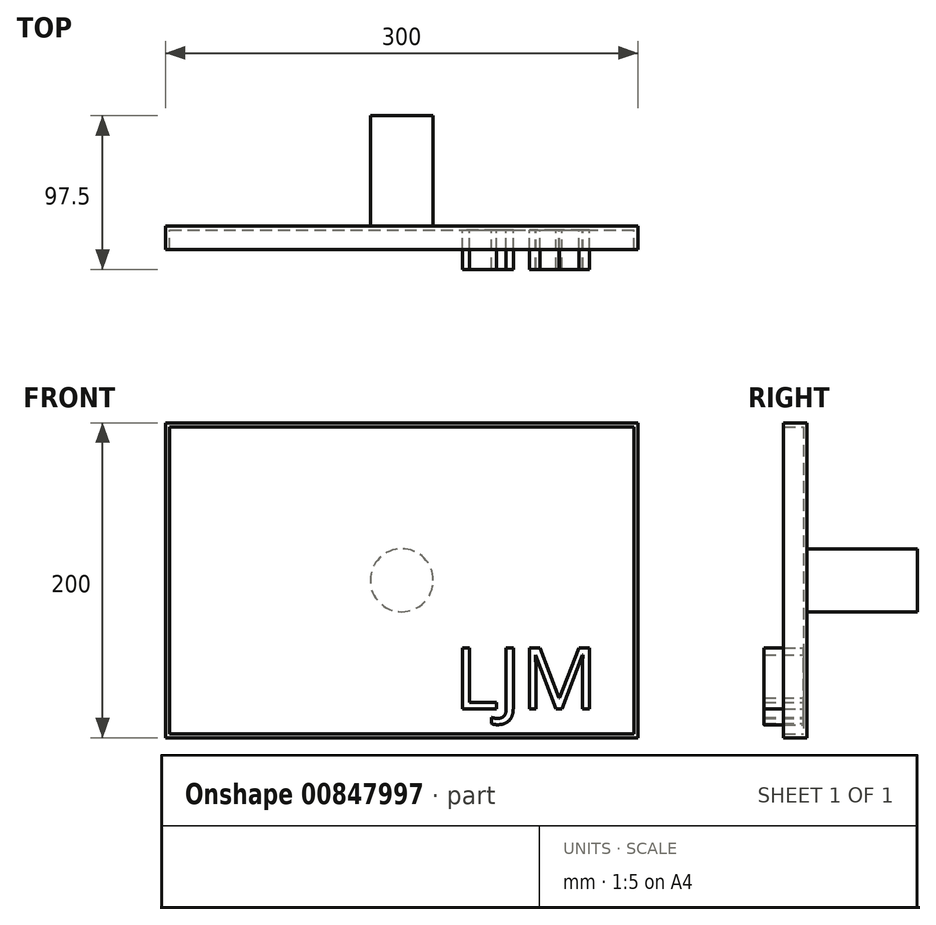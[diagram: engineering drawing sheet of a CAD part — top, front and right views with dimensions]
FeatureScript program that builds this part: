
annotation { "Feature Type Name" : "Feature", "Feature Type Description" : "" }
export const myFeature = defineFeature(function(context is Context, id is Id, definition is map)
    precondition{}
    {
        {
            var Q0;
            Q0=qCreatedBy(makeId("Front.planeOp"),FACE);
            var sketch = newSketch(context, id + "F0", { "sketchPlane" : qUnion([Q0])});
            skLineSegment(sketch, "E0.bottom", {"start": v(-150, 100) * mm, "end": v(150, 100) * mm});
            skLineSegment(sketch, "E0.top", {"start": v(-150, -100) * mm, "end": v(150, -100) * mm});
            skLineSegment(sketch, "E0.left", {"start": v(-150, 100) * mm, "end": v(-150, -100) * mm});
            skLineSegment(sketch, "E0.right", {"start": v(150, 100) * mm, "end": v(150, -100) * mm});
            skLineSegment(sketch, "E1", {"start": v(0, 0) * mm, "end": v(0, 116.1) * mm});
            skSolve(sketch);
        }
        {
            var Q0;
            Q0=makeQuery(id+"F0.imprint","IMPRINT",FACE,{"disambiguationData":[TD([[makeQuery(id+"F0.imprint","IMPRINT",EDGE,{"derivedFrom":sQuery(id+"F0.wireOp",EDGE,"E0.bottom")}),-1.0]])]});
            extrude(context, id + "F1", {"entities" : qUnion([Q0]), "depth" : 15 * mm, "offsetDistance" : 25 * mm});
        }
        {
            var Q0;
            Q0=makeQuery(id+"F1.opExtrude","CAP_FACE",FACE,{"disambiguationData":[OSD([sQuery(id+"F0.wireOp",EDGE,"E0.bottom"),sQuery(id+"F0.wireOp",EDGE,"E0.top"),sQuery(id+"F0.wireOp",EDGE,"E0.left"),sQuery(id+"F0.wireOp",EDGE,"E0.right")])],"isStart":false});
            shell(context, id + "F2", {"entities" : qUnion([Q0]), "thickness" : 2.5 * mm});
        }
        {
            var Q0;
            Q0=makeQuery(id+"F2.opShell","OFFSET_FACE",FACE,{"disambiguationData":[OSD([sQuery(id+"F0.wireOp",EDGE,"E0.bottom"),sQuery(id+"F0.wireOp",EDGE,"E0.top"),sQuery(id+"F0.wireOp",EDGE,"E0.left"),sQuery(id+"F0.wireOp",EDGE,"E0.right")])]});
            var sketch = newSketch(context, id + "F3", { "sketchPlane" : qUnion([Q0])});
            skText(sketch, "E2", { "text": "LJM", "fontName": "OpenSans-Regular.ttf"});
            const initialGuessF3  = {"E2": [0.03333, -0.08161, 1, 0, 0.03885]};
            skSetInitialGuess(sketch, initialGuessF3);
            skSolve(sketch);
        }
        {
            var Q0;
            Q0 = qSketchRegion(id + "F3", true);
            extrude(context, id + "F4", {"entities" : qUnion([Q0]), "operationType" : NewBodyOperationType.ADD, "depth" : 25 * mm, "offsetDistance" : 25 * mm});
        }
        {
            var Q0;
            Q0=makeQuery(id+"F1.opExtrude","CAP_FACE",FACE,{"disambiguationData":[OSD([sQuery(id+"F0.wireOp",EDGE,"E0.bottom"),sQuery(id+"F0.wireOp",EDGE,"E0.top"),sQuery(id+"F0.wireOp",EDGE,"E0.left"),sQuery(id+"F0.wireOp",EDGE,"E0.right")])],"isStart":true});
            var sketch = newSketch(context, id + "F5", { "sketchPlane" : qUnion([Q0])});
            skPoint(sketch, "E3", {"position": v(0, 100) * mm});
            skPoint(sketch, "E4", {"position": v(150, 0) * mm});
            skPoint(sketch, "E5.center.orphan", {"position": v(0, 0) * mm});
            skCircle(sketch, "E6", {"center": v(0, 0) * mm, "radius": 20 * mm});
            skSolve(sketch);
        }
        {
            var Q0;
            Q0=makeQuery(id+"F5.imprint","IMPRINT",FACE,{"disambiguationData":[TD([[makeQuery(id+"F5.imprint","IMPRINT",EDGE,{"derivedFrom":sQuery(id+"F5.wireOp",EDGE,"E6")}),1.0]])]});
            var Q1;
            Q1=sQuery(id+"F5.wireOp",EDGE,"E6");
            extrude(context, id + "F6", {"entities" : qUnion([Q0]), "operationType" : NewBodyOperationType.ADD, "surfaceEntities" : qUnion([Q1]), "depth" : 70 * mm, "offsetDistance" : 25 * mm});
        }
    });
